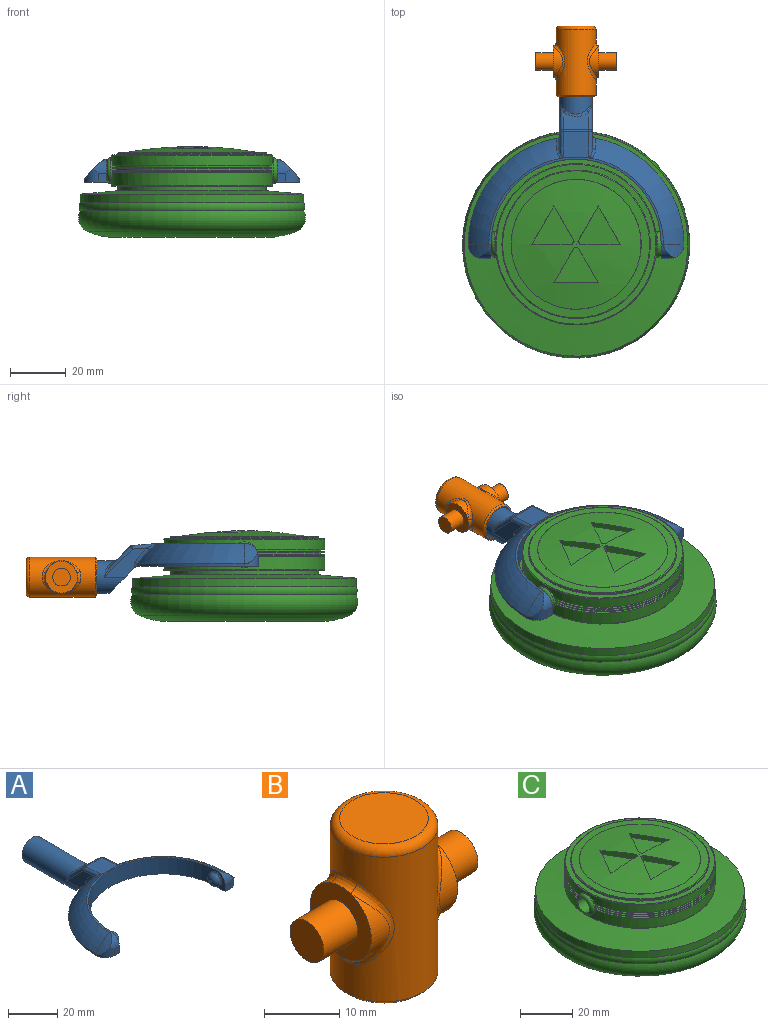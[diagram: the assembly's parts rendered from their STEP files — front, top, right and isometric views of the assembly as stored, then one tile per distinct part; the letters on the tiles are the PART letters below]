
ASSEMBLY  parts=3 mates=2
PART A: 48 faces, bbox 77.3x80.8x18.2 mm
  f0: plane 11.99x9.83mm, normal (0,-0.71,-0.71), area 141.5mm2, adj f1,f2,f9,f30,f43,f46
  f1: plane 15.39x10.49mm, normal (-1,0,0), area 63.5mm2, adj f0,f30,f32,f36,f46,f47
  f2: plane 15.39x10.49mm, normal (1,0,0), area 63.5mm2, adj f0,f30,f34,f39,f43,f44
  f3: plane 9.14x6.37mm, normal (0,0.71,0.71), area 67.6mm2, adj f35,f36,f39,f40
  f4: cylinder r=38.61mm len=37.99mm, axis (0,0,-1), area 42.6mm2, adj f6,f9,f17,f46,f47
  f5: torus R=19.3mm, axis (0,0,-1), area 507.8mm2, adj f10,f11,f12,f29,f42,f44
  f6: torus R=19.3mm, axis (0,0,-1), area 507.8mm2, adj f4,f11,f15,f28,f45,f47
  f7: cylinder r=30.48mm len=60.96mm, axis (0,0,-1), area 746.6mm2, adj f8,f9,f11,f14,f21,f24
  f8: plane 8.13x5.08mm, normal (-1,0,0), area 19.9mm2, adj f7,f9,f13,f19,f24
  f9: plane 77.22x43.73mm, normal (0,0,-1), area 956.2mm2, adj f0,f4,f7,f8,f10,f13,f14,f16
  f10: cylinder r=38.61mm len=37.99mm, axis (0,0,-1), area 42.6mm2, adj f5,f9,f20,f43,f44
  f11: plane 62.55x30.95mm, normal (0,0,1), area 75mm2, adj f5,f6,f7,f18,f19,f27
  f12: cylinder r=22.71mm len=7.33mm, axis (0,1,0), area 24.8mm2, adj f5,f19,f20
  f13: plane 3.05x3.05mm, normal (0,-1,0), area 9.3mm2, adj f8,f9,f19,f20
  f14: plane 8.13x5.08mm, normal (1,0,0), area 19.9mm2, adj f7,f9,f16,f18,f21
  f15: cylinder r=22.71mm len=7.33mm, axis (0,1,0), area 24.8mm2, adj f6,f17,f18
  f16: plane 3.05x3.05mm, normal (0,-1,0), area 9.3mm2, adj f9,f14,f17,f18
  f17: cylinder r=5.08mm len=5.08mm, axis (0,0,-1), area 21.9mm2, adj f4,f9,f15,f16,f18
  f18: cylinder r=5.08mm len=5.08mm, axis (-1,0,0), area 21.9mm2, adj f11,f14,f15,f16,f17
  f19: cylinder r=5.08mm len=5.08mm, axis (-1,0,0), area 21.9mm2, adj f8,f11,f12,f13,f20
  f20: cylinder r=5.08mm len=5.08mm, axis (0,0,-1), area 21.9mm2, adj f9,f10,f12,f13,f19
  f21: cylinder r=3.17mm len=6.35mm, axis (-1,0,0), area 12.7mm2, adj f7,f14,f23
  f22: plane 1.27x1.27mm, normal (1,0,0), area 1.3mm2, adj f23
  f23: torus R=0.64mm, axis (1,0,0), area 56.5mm2, adj f21,f22
  f24: cylinder r=3.17mm len=6.35mm, axis (1,0,0), area 12.7mm2, adj f7,f8,f26
  f25: plane 1.27x1.27mm, normal (-1,0,0), area 1.3mm2, adj f26
  f26: torus R=0.64mm, axis (-1,0,0), area 56.5mm2, adj f24,f25
  f27: plane 9.86x9.36mm, normal (0,0.09,1), area 85.6mm2, adj f11,f28,f29,f32,f34,f35,f42,f45
  f28: plane 1.04x0.17mm, normal (0,-1,0), area 0mm2, adj f6,f27,f45
  f29: plane 1.04x0.17mm, normal (0,-1,0), area 0mm2, adj f5,f27,f42
  f30: cylinder r=5.84mm len=33.01mm, axis (0,-1,0), area 1029.7mm2, adj f0,f1,f2,f31,f38,f40,f41
  f31: plane 11.68x11.68mm, normal (0,1,0), area 107.2mm2, adj f30
  f32: cylinder r=1.27mm len=9.13mm, axis (0,-1,0.09), area 14.4mm2, adj f1,f27,f33,f45
  f33: sphere r=1.27mm, area 1.5mm2, adj f32,f35,f36
  f34: cylinder r=1.27mm len=9.13mm, axis (0,1,-0.09), area 14.4mm2, adj f2,f27,f37,f42
  f35: cylinder r=1.27mm len=9.14mm, axis (-1,0,0), area 8.1mm2, adj f3,f27,f33,f37
  f36: cylinder r=1.27mm len=10.91mm, axis (0,-0.71,0.71), area 23.1mm2, adj f1,f3,f33,f38
  f37: sphere r=1.27mm, area 1.5mm2, adj f34,f35,f39
  f38: bspline ~4.55x2.75mm, area 2.3mm2, adj f30,f36,f40
  f39: cylinder r=1.27mm len=10.91mm, axis (0,0.71,-0.71), area 23.1mm2, adj f2,f3,f37,f41
  f40: bspline ~9.14x2.56mm, area 10.7mm2, adj f3,f30,f38,f41
  f41: bspline ~5.23x3.53mm, area 2.3mm2, adj f30,f39,f40
  f42: bspline ~4.62x3.14mm, area 5.2mm2, adj f5,f27,f29,f34,f44
  f43: cylinder r=1.27mm len=1.74mm, axis (0,0,-1), area 1.9mm2, adj f0,f2,f9,f10,f44
  f44: bspline ~8.6x7.86mm, area 11.9mm2, adj f2,f5,f10,f42,f43
  f45: bspline ~4.62x3.14mm, area 5.2mm2, adj f6,f27,f28,f32,f47
  f46: cylinder r=1.27mm len=1.74mm, axis (0,0,-1), area 1.9mm2, adj f0,f1,f4,f9,f47
  f47: bspline ~8.6x7.86mm, area 11.9mm2, adj f1,f4,f6,f45,f46
PART B: 25 faces, bbox 28.9x15.5x25.4 mm
  f0: cylinder r=5.71mm len=10.81mm, axis (-1,0,0), area 26.2mm2, adj f5,f15
  f1: cylinder r=5.71mm len=10.81mm, axis (-1,0,0), area 26.2mm2, adj f8,f11
  f2: cylinder r=7.14mm len=23.5mm, axis (0,0,-1), area 763.2mm2, adj f9,f10,f11,f12,f13,f14,f15,f16
  f3: plane 11.75x11.75mm, normal (0,0,1), area 108.4mm2, adj f17
  f4: plane 13.02x13.02mm, normal (0,0,-1), area 16.3mm2, adj f22,f24
  f5: plane 11.46x11.46mm, normal (1,0,0), area 70.9mm2, adj f0,f6,f13,f16,f18
  f6: cylinder r=5.71mm len=10.81mm, axis (-1,0,0), area 26.2mm2, adj f5,f14
  f7: cylinder r=5.71mm len=10.81mm, axis (-1,0,0), area 26.2mm2, adj f8,f10
  f8: plane 11.46x11.46mm, normal (-1,0,0), area 70.9mm2, adj f1,f7,f9,f12,f20
  f9: bspline ~4.64x1.73mm, area 6.5mm2, adj f2,f8,f10,f11
  f10: bspline ~13.62x4.91mm, area 20.7mm2, adj f2,f7,f9,f12
  f11: bspline ~13.6x4.87mm, area 20.7mm2, adj f1,f2,f9,f12
  f12: bspline ~4.64x1.73mm, area 6.5mm2, adj f2,f8,f10,f11
  f13: bspline ~4.64x1.73mm, area 6.5mm2, adj f2,f5,f14,f15
  f14: bspline ~13.62x4.91mm, area 20.7mm2, adj f2,f6,f13,f16
  f15: bspline ~13.6x4.87mm, area 20.7mm2, adj f0,f2,f13,f16
  f16: bspline ~4.64x1.73mm, area 6.5mm2, adj f2,f5,f14,f15
  f17: torus R=5.87mm, axis (0,0,1), area 83.8mm2, adj f2,f3
  f18: cylinder r=3.17mm len=6.35mm, axis (-1,0,0), area 126.7mm2, adj f5,f19
  f19: plane 6.35x6.35mm, normal (1,0,0), area 31.7mm2, adj f18
  f20: cylinder r=3.17mm len=6.35mm, axis (1,0,0), area 126.7mm2, adj f8,f21
  f21: plane 6.35x6.35mm, normal (-1,0,0), area 31.7mm2, adj f20
  f22: cylinder r=6.1mm len=22.86mm, axis (0,0,-1), area 875.6mm2, adj f4,f23
  f23: plane 12.19x12.19mm, normal (0,0,-1), area 116.7mm2, adj f22
  f24: cone r=7.14mm half-angle=45deg, axis (0,0,1), area 38.5mm2, adj f2,f4
PART C: 63 faces, bbox 96.2x96.2x32.5 mm
  f0: cylinder r=28.85mm len=57.71mm, axis (0,0,-1), area 771.7mm2, adj f3,f4,f53,f54,f59
  f1: plane 56.98x24.29mm, normal (0,0,-1), area 98.8mm2, adj f6,f8,f53,f54
  f2: plane 56.98x24.29mm, normal (0,0,-1), area 98.8mm2, adj f5,f7,f53,f54
  f3: plane 57x24.36mm, normal (0,0,1), area 99mm2, adj f0,f6,f53,f54
  f4: plane 57x24.36mm, normal (0,0,1), area 99mm2, adj f0,f5,f53,f54
  f5: cylinder r=27.61mm len=54.49mm, axis (0,0,-1), area 49.3mm2, adj f2,f4,f53,f54
  f6: cylinder r=27.61mm len=54.49mm, axis (0,0,-1), area 49.3mm2, adj f1,f3,f53,f54
  f7: cylinder r=28.85mm len=56.98mm, axis (0,0,-1), area 25.9mm2, adj f2,f10,f53,f54
  f8: cylinder r=28.85mm len=56.98mm, axis (0,0,-1), area 25.9mm2, adj f1,f9,f53,f54
  f9: plane 56.98x24.28mm, normal (0,0,1), area 98.8mm2, adj f8,f14,f53,f54
  f10: plane 56.98x24.28mm, normal (0,0,1), area 98.8mm2, adj f7,f13,f53,f54
  f11: plane 57x24.35mm, normal (0,0,-1), area 99mm2, adj f14,f16,f53,f54
  f12: plane 57x24.35mm, normal (0,0,-1), area 99mm2, adj f13,f15,f53,f54
  f13: cylinder r=27.61mm len=54.48mm, axis (0,0,-1), area 49.3mm2, adj f10,f12,f53,f54
  f14: cylinder r=27.61mm len=54.48mm, axis (0,0,-1), area 49.3mm2, adj f9,f11,f53,f54
  f15: cylinder r=28.85mm len=57.02mm, axis (0,0,-1), area 25.9mm2, adj f12,f20,f53,f54
  f16: cylinder r=28.85mm len=57.02mm, axis (0,0,-1), area 25.9mm2, adj f11,f19,f53,f54
  f17: plane 57.08x24.61mm, normal (0,0,-1), area 99.7mm2, adj f22,f23,f53,f54
  f18: plane 57.08x24.61mm, normal (0,0,-1), area 99.7mm2, adj f21,f23,f53,f54
  f19: plane 57.02x24.41mm, normal (0,0,1), area 99.2mm2, adj f16,f22,f53,f54
  f20: plane 57.02x24.41mm, normal (0,0,1), area 99.2mm2, adj f15,f21,f53,f54
  f21: cylinder r=27.61mm len=54.57mm, axis (0,0,-1), area 49.5mm2, adj f18,f20,f53,f54
  f22: cylinder r=27.61mm len=54.57mm, axis (0,0,-1), area 49.5mm2, adj f17,f19,f53,f54
  f23: cylinder r=28.85mm len=57.71mm, axis (0,0,-1), area 627.5mm2, adj f17,f18,f53,f54,f60
  f24: sphere r=135.39mm, area 1385.3mm2, adj f37,f38,f39,f40,f42,f43,f44,f45
  f25: plane 39.33x39.33mm, normal (0,0,-1), area 1214.6mm2, adj f26
  f26: torus R=20.12mm, axis (0,0,-1), area 1429.3mm2, adj f25,f27
  f27: torus R=27.74mm, axis (0,0,-1), area 3542.1mm2, adj f26,f28
  f28: torus R=35.36mm, axis (0,0,-1), area 2180.1mm2, adj f27,f29
  f29: torus R=37.35mm, axis (0,0,-1), area 734.6mm2, adj f28,f30
  f30: cylinder r=40.06mm len=80.11mm, axis (0,0,-1), area 799.1mm2, adj f29,f31
  f31: cone r=26.57mm half-angle=85deg, axis (0,0,-1), area 2833.8mm2, adj f30,f32
  f32: cylinder r=26.57mm len=53.14mm, axis (0,0,-1), area 265mm2, adj f31,f33
  f33: plane 57.2x57.2mm, normal (0,0,-1), area 352.2mm2, adj f32,f59
  f34: cone r=26.57mm half-angle=87deg, axis (0,0,-1), area 475.4mm2, adj f61,f62
  f35: cylinder r=26.57mm len=53.14mm, axis (0,0,-1), area 92.3mm2, adj f36,f61
  f36: plane 57.2x57.2mm, normal (0,0,1), area 352.2mm2, adj f35,f60
  f37: plane 13.75x7.94mm, normal (0.87,-0.5,0), area 28mm2, adj f24,f38,f40,f41
  f38: plane 14.61x2.53mm, normal (0,1,0), area 32.2mm2, adj f24,f37,f39,f41
  f39: cylinder r=1.27mm len=2.53mm, axis (0,0,1), area 3.4mm2, adj f24,f38,f40,f41
  f40: plane 12.65x7.3mm, normal (-0.87,-0.5,0), area 32.2mm2, adj f24,f37,f39,f41
  f41: plane 15.24x13.75mm, normal (0,0,1), area 108.3mm2, adj f37,f38,f39,f40
  f42: plane 13.75x7.94mm, normal (-0.87,-0.5,0), area 28mm2, adj f24,f43,f45,f46
  f43: plane 12.65x7.3mm, normal (0.87,-0.5,0), area 32.2mm2, adj f24,f42,f44,f46
  f44: cylinder r=1.27mm len=2.53mm, axis (0,0,1), area 3.4mm2, adj f24,f43,f45,f46
  f45: plane 14.61x2.53mm, normal (0,1,0), area 32.2mm2, adj f24,f42,f44,f46
  f46: plane 15.24x13.75mm, normal (0,0,1), area 108.3mm2, adj f42,f43,f44,f45
  f47: plane 12.65x7.3mm, normal (0.87,-0.5,0), area 32.2mm2, adj f24,f48,f50,f51
  f48: plane 15.88x1.84mm, normal (0,1,0), area 28mm2, adj f24,f47,f49,f51
  f49: plane 12.65x7.3mm, normal (-0.87,-0.5,0), area 32.2mm2, adj f24,f48,f50,f51
  f50: cylinder r=1.27mm len=2.53mm, axis (0,0,1), area 3.4mm2, adj f24,f47,f49,f51
  f51: plane 15.88x12.65mm, normal (0,0,1), area 108.3mm2, adj f47,f48,f49,f50
  f52: plane 6.6x6.6mm, normal (1,0,0), area 2.6mm2, adj f57,f58
  f53: cylinder r=4.57mm len=9.14mm, axis (-1,0,0), area 20.3mm2, adj f0,f1,f2,f3,f4,f5,f6,f7
  f54: cylinder r=4.57mm len=9.14mm, axis (-1,0,0), area 20.3mm2, adj f0,f1,f2,f3,f4,f5,f6,f7
  f55: plane 6.6x6.6mm, normal (-1,0,0), area 2.6mm2, adj f56,f58
  f56: torus R=3.3mm, axis (1,0,0), area 51.5mm2, adj f54,f55
  f57: torus R=3.3mm, axis (1,0,0), area 51.5mm2, adj f52,f53
  f58: cylinder r=3.17mm len=60.96mm, axis (1,0,0), area 1216.1mm2, adj f52,f55
  f59: torus R=28.6mm, axis (0,0,1), area 72.1mm2, adj f0,f33
  f60: torus R=28.6mm, axis (0,0,-1), area 72.1mm2, adj f23,f36
  f61: torus R=26.31mm, axis (0,0,1), area 64.2mm2, adj f34,f35
  f62: torus R=23.29mm, axis (0,0,1), area 4.5mm2, adj f24,f34
PLACE A t=(32.34,27.52,20.85)mm
PLACE B rot(axis=(-1,0,0),90deg) t=(32.34,80.3,16.88)mm
PLACE C t=(32.34,27.52,33.52)mm
MATE revolute A.f24 <-> C.f53  axis (-1,0,0) through (62.82,27.52,24.92)mm
MATE revolute B.f2 <-> A.f30  axis (0,-1,0) through (32.34,103.16,16.88)mm
